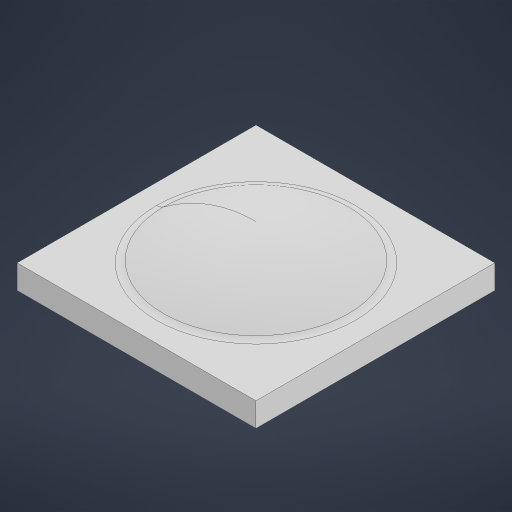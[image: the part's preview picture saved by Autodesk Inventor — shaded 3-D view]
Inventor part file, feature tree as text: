
AUTODESK INVENTOR PART (.ipt)
format: ipt  version: 2024.3 (Build 283343000, 343)  size: 233,984 bytes
history: native  units: mm
features: sketch x2, extrude x1, revolve x1, fillet x1
ambient origin geometry x8: Origin, YZ Plane, XZ Plane, XY Plane, X Axis, Y Axis, Z Axis, Center Point
bodies: Solid1 (feature_tree)
feature tree (5):
  sketch  "Sketch1"  dims[d0=100.0mm d1=30.0mm]
  sketch  "Sketch2"  dims[d2=10.0mm d3=10.0mm d4=0.0mm d6=90.0deg d7=5.0mm]
  extrude  "Extrusion1"  Depth=30.0mm
  revolve  "Revolution2"  [1 undecoded]
  fillet  "Fillet1"  [1 undecoded]
note: 2 required parameter values undecoded (feature->parameter linkage not recoverable at this tier; creation-order binding heuristic only, values carry confidence <= 0.55)